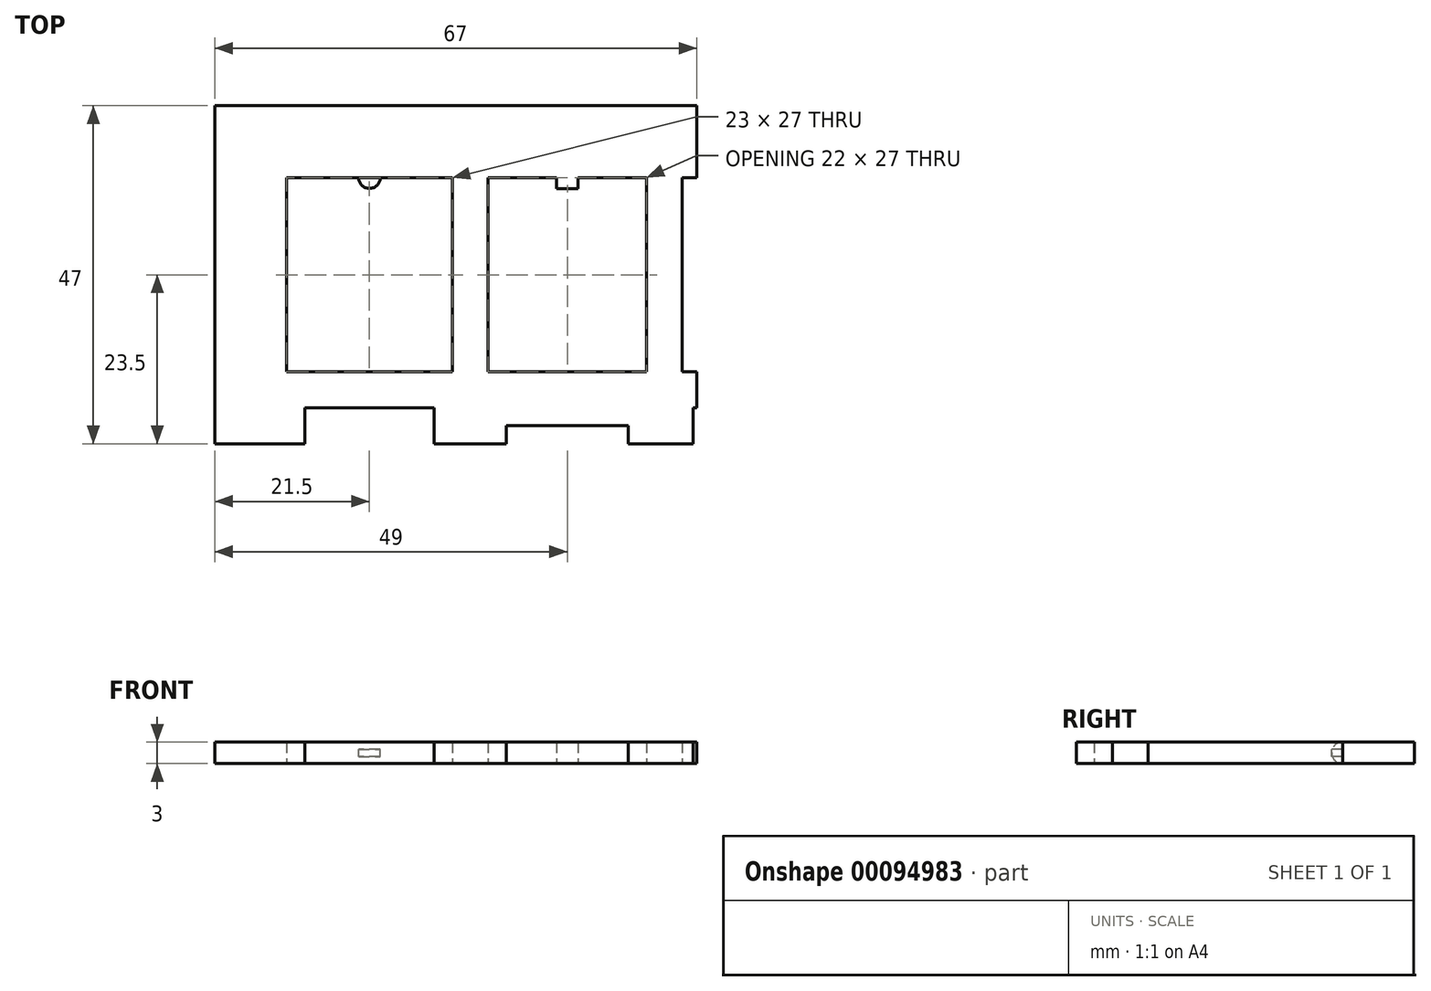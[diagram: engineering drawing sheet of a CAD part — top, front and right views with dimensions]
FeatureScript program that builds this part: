
annotation { "Feature Type Name" : "Feature", "Feature Type Description" : "" }
export const myFeature = defineFeature(function(context is Context, id is Id, definition is map)
    precondition{}
    {
        {
            var Q0;
            Q0=qCreatedBy(makeId("Top.planeOp"),FACE);
            var sketch = newSketch(context, id + "F0", { "sketchPlane" : qUnion([Q0])});
            skLineSegment(sketch, "E0.bottom", {"start": v(59.5, -71.5) * mm, "end": v(-59.5, -71.5) * mm});
            skLineSegment(sketch, "E0.top", {"start": v(59.5, 71.5) * mm, "end": v(-59.5, 71.5) * mm});
            skLineSegment(sketch, "E0.left", {"start": v(59.5, -71.5) * mm, "end": v(59.5, 71.5) * mm});
            skLineSegment(sketch, "E0.right", {"start": v(-59.5, -71.5) * mm, "end": v(-59.5, 71.5) * mm});
            skPoint(sketch, "E0.middle", {"position": v(0, 0) * mm});
            skLineSegment(sketch, "E1.bottom", {"start": v(-26.5, 34.5) * mm, "end": v(-49.5, 34.5) * mm});
            skLineSegment(sketch, "E1.top", {"start": v(-26.5, 61.5) * mm, "end": v(-49.5, 61.5) * mm});
            skLineSegment(sketch, "E1.left", {"start": v(-26.5, 34.5) * mm, "end": v(-26.5, 61.5) * mm});
            skLineSegment(sketch, "E1.right", {"start": v(-49.5, 34.5) * mm, "end": v(-49.5, 61.5) * mm});
            skPoint(sketch, "E1.middle", {"position": v(-38, 48) * mm});
            skLineSegment(sketch, "E2.bottom", {"start": v(0.5, 34.5) * mm, "end": v(-21.5, 34.5) * mm});
            skLineSegment(sketch, "E2.top", {"start": v(0.5, 61.5) * mm, "end": v(-21.5, 61.5) * mm});
            skLineSegment(sketch, "E2.left", {"start": v(0.5, 34.5) * mm, "end": v(0.5, 61.5) * mm});
            skLineSegment(sketch, "E2.right", {"start": v(-21.5, 34.5) * mm, "end": v(-21.5, 61.5) * mm});
            skPoint(sketch, "E2.middle", {"position": v(-10.5, 48) * mm});
            skLineSegment(sketch, "E3.bottom", {"start": v(5.5, 61.5) * mm, "end": v(26.5, 61.5) * mm});
            skLineSegment(sketch, "E3.top", {"start": v(5.5, 34.5) * mm, "end": v(26.5, 34.5) * mm});
            skLineSegment(sketch, "E3.left", {"start": v(5.5, 61.5) * mm, "end": v(5.5, 34.5) * mm});
            skLineSegment(sketch, "E3.right", {"start": v(26.5, 61.5) * mm, "end": v(26.5, 34.5) * mm});
            skLineSegment(sketch, "E4.bottom", {"start": v(31.5, 61.5) * mm, "end": v(49.5, 61.5) * mm});
            skLineSegment(sketch, "E4.top", {"start": v(31.5, 34.5) * mm, "end": v(49.5, 34.5) * mm});
            skLineSegment(sketch, "E4.left", {"start": v(31.5, 61.5) * mm, "end": v(31.5, 34.5) * mm});
            skLineSegment(sketch, "E4.right", {"start": v(49.5, 61.5) * mm, "end": v(49.5, 34.5) * mm});
            skLineSegment(sketch, "E5.bottom", {"start": v(33, 27) * mm, "end": v(48, 27) * mm});
            skLineSegment(sketch, "E5.top", {"start": v(33, 5) * mm, "end": v(48, 5) * mm});
            skLineSegment(sketch, "E5.left", {"start": v(33, 27) * mm, "end": v(33, 5) * mm});
            skLineSegment(sketch, "E5.right", {"start": v(48, 27) * mm, "end": v(48, 5) * mm});
            skPoint(sketch, "E6", {"position": v(40.5, 48) * mm});
            skPoint(sketch, "E6.positionSnap0", {"position": v(40.5, 34.5) * mm});
            skPoint(sketch, "E6.positionSnap1", {"position": v(49.5, 48) * mm});
            skPoint(sketch, "E7", {"position": v(16, 48) * mm});
            skPoint(sketch, "E7.positionSnap0", {"position": v(16, 34.5) * mm});
            skPoint(sketch, "E8", {"position": v(40.5, 16) * mm});
            skPoint(sketch, "E8.positionSnap0", {"position": v(40.5, 5) * mm});
            skPoint(sketch, "E8.positionSnap1", {"position": v(48, 16) * mm});
            skLineSegment(sketch, "E9.bottom", {"start": v(-19, 27) * mm, "end": v(-2, 27) * mm});
            skLineSegment(sketch, "E9.top", {"start": v(-19, 5) * mm, "end": v(-2, 5) * mm});
            skLineSegment(sketch, "E9.left", {"start": v(-19, 27) * mm, "end": v(-19, 5) * mm});
            skLineSegment(sketch, "E9.right", {"start": v(-2, 27) * mm, "end": v(-2, 5) * mm});
            skPoint(sketch, "E10", {"position": v(-10.5, 16) * mm});
            skPoint(sketch, "E10.positionSnap0", {"position": v(-2, 16) * mm});
            skPoint(sketch, "E10.positionSnap1", {"position": v(-10.5, 5) * mm});
            skLineSegment(sketch, "E11.bottom", {"start": v(-47, 29.5) * mm, "end": v(-29, 29.5) * mm});
            skLineSegment(sketch, "E11.top", {"start": v(-47, 2.5) * mm, "end": v(-29, 2.5) * mm});
            skLineSegment(sketch, "E11.left", {"start": v(-47, 29.5) * mm, "end": v(-47, 2.5) * mm});
            skLineSegment(sketch, "E11.right", {"start": v(-29, 29.5) * mm, "end": v(-29, 2.5) * mm});
            skPoint(sketch, "E12", {"position": v(-38, 16) * mm});
            skPoint(sketch, "E12.positionSnap0", {"position": v(-29, 16) * mm});
            skPoint(sketch, "E12.positionSnap1", {"position": v(-38, 2.5) * mm});
            skLineSegment(sketch, "E13.bottom", {"start": v(7, 29.5) * mm, "end": v(25, 29.5) * mm});
            skLineSegment(sketch, "E13.top", {"start": v(7, 2.5) * mm, "end": v(25, 2.5) * mm});
            skLineSegment(sketch, "E13.left", {"start": v(7, 29.5) * mm, "end": v(7, 2.5) * mm});
            skLineSegment(sketch, "E13.right", {"start": v(25, 29.5) * mm, "end": v(25, 2.5) * mm});
            skPoint(sketch, "E14", {"position": v(16, 16) * mm});
            skPoint(sketch, "E14.positionSnap0", {"position": v(25, 16) * mm});
            skPoint(sketch, "E14.positionSnap1", {"position": v(16, 2.5) * mm});
            skLineSegment(sketch, "E15.bottom", {"start": v(-45, -5) * mm, "end": v(-31, -5) * mm});
            skLineSegment(sketch, "E15.top", {"start": v(-45, -27) * mm, "end": v(-31, -27) * mm});
            skLineSegment(sketch, "E15.left", {"start": v(-45, -5) * mm, "end": v(-45, -27) * mm});
            skLineSegment(sketch, "E15.right", {"start": v(-31, -5) * mm, "end": v(-31, -27) * mm});
            skLineSegment(sketch, "E16.bottom", {"start": v(9.58, -5) * mm, "end": v(22.58, -5) * mm});
            skLineSegment(sketch, "E16.top", {"start": v(9.58, -27) * mm, "end": v(22.58, -27) * mm});
            skLineSegment(sketch, "E16.left", {"start": v(9.58, -5) * mm, "end": v(9.58, -27) * mm});
            skLineSegment(sketch, "E16.right", {"start": v(22.58, -5) * mm, "end": v(22.58, -27) * mm});
            skPoint(sketch, "E17.firstSnap0", {"position": v(16.08, -5) * mm});
            skLineSegment(sketch, "E17.bottom", {"start": v(34.82, -5) * mm, "end": v(47.82, -5) * mm});
            skLineSegment(sketch, "E17.top", {"start": v(34.82, -27) * mm, "end": v(47.82, -27) * mm});
            skLineSegment(sketch, "E17.left", {"start": v(34.82, -5) * mm, "end": v(34.82, -27) * mm});
            skLineSegment(sketch, "E17.right", {"start": v(47.82, -5) * mm, "end": v(47.82, -27) * mm});
            skPoint(sketch, "E18", {"position": v(-38, -16) * mm});
            skPoint(sketch, "E18.positionSnap0", {"position": v(-31, -16) * mm});
            skPoint(sketch, "E18.positionSnap1", {"position": v(-38, -27) * mm});
            skPoint(sketch, "E19", {"position": v(16.08, -16) * mm});
            skPoint(sketch, "E19.positionSnap0", {"position": v(22.58, -16) * mm});
            skPoint(sketch, "E19.positionSnap1", {"position": v(16.08, -27) * mm});
            skPoint(sketch, "E20", {"position": v(41.32, -16) * mm});
            skPoint(sketch, "E20.positionSnap0", {"position": v(47.82, -16) * mm});
            skPoint(sketch, "E20.positionSnap1", {"position": v(41.32, -27) * mm});
            skLineSegment(sketch, "E21.bottom", {"start": v(-17, -5) * mm, "end": v(-4, -5) * mm});
            skLineSegment(sketch, "E21.top", {"start": v(-17, -27) * mm, "end": v(-4, -27) * mm});
            skLineSegment(sketch, "E21.left", {"start": v(-17, -5) * mm, "end": v(-17, -27) * mm});
            skLineSegment(sketch, "E21.right", {"start": v(-4, -5) * mm, "end": v(-4, -27) * mm});
            skPoint(sketch, "E22", {"position": v(-10.5, -16) * mm});
            skPoint(sketch, "E22.positionSnap0", {"position": v(-4, -16) * mm});
            skPoint(sketch, "E22.positionSnap1", {"position": v(-10.5, -27) * mm});
            skLineSegment(sketch, "E23.bottom", {"start": v(-44.5, -37) * mm, "end": v(-31.5, -37) * mm});
            skLineSegment(sketch, "E23.top", {"start": v(-44.5, -59) * mm, "end": v(-31.5, -59) * mm});
            skLineSegment(sketch, "E23.left", {"start": v(-44.5, -37) * mm, "end": v(-44.5, -59) * mm});
            skLineSegment(sketch, "E23.right", {"start": v(-31.5, -37) * mm, "end": v(-31.5, -59) * mm});
            skLineSegment(sketch, "E24.bottom", {"start": v(-17, -37) * mm, "end": v(-4, -37) * mm});
            skLineSegment(sketch, "E24.top", {"start": v(-17, -59) * mm, "end": v(-4, -59) * mm});
            skLineSegment(sketch, "E24.left", {"start": v(-17, -37) * mm, "end": v(-17, -59) * mm});
            skLineSegment(sketch, "E24.right", {"start": v(-4, -37) * mm, "end": v(-4, -59) * mm});
            skLineSegment(sketch, "E25.bottom", {"start": v(9.58, -37) * mm, "end": v(22.58, -37) * mm});
            skLineSegment(sketch, "E25.top", {"start": v(9.58, -59) * mm, "end": v(22.58, -59) * mm});
            skLineSegment(sketch, "E25.left", {"start": v(9.58, -37) * mm, "end": v(9.58, -59) * mm});
            skLineSegment(sketch, "E25.right", {"start": v(22.58, -37) * mm, "end": v(22.58, -59) * mm});
            skLineSegment(sketch, "E26.bottom", {"start": v(34.82, -37) * mm, "end": v(47.82, -37) * mm});
            skLineSegment(sketch, "E26.top", {"start": v(34.82, -59) * mm, "end": v(47.82, -59) * mm});
            skLineSegment(sketch, "E26.left", {"start": v(34.82, -37) * mm, "end": v(34.82, -59) * mm});
            skLineSegment(sketch, "E26.right", {"start": v(47.82, -37) * mm, "end": v(47.82, -59) * mm});
            skPoint(sketch, "E27", {"position": v(-38, -48) * mm});
            skPoint(sketch, "E27.positionSnap0", {"position": v(-31.5, -48) * mm});
            skPoint(sketch, "E27.positionSnap1", {"position": v(-38, -59) * mm});
            skPoint(sketch, "E28", {"position": v(-10.5, -48) * mm});
            skPoint(sketch, "E28.positionSnap0", {"position": v(-10.5, -59) * mm});
            skPoint(sketch, "E28.positionSnap1", {"position": v(-4, -48) * mm});
            skPoint(sketch, "E29", {"position": v(16.08, -48) * mm});
            skPoint(sketch, "E29.positionSnap0", {"position": v(22.58, -48) * mm});
            skPoint(sketch, "E29.positionSnap1", {"position": v(16.08, -59) * mm});
            skPoint(sketch, "E30", {"position": v(41.32, -48) * mm});
            skPoint(sketch, "E30.positionSnap0", {"position": v(47.82, -48) * mm});
            skPoint(sketch, "E30.positionSnap1", {"position": v(41.32, -59) * mm});
            skPoint(sketch, "E31", {"position": v(-44.5, -49.5) * mm});
            skPoint(sketch, "E32", {"position": v(-17, -48.5) * mm});
            skPoint(sketch, "E33", {"position": v(9.58, -48.5) * mm});
            skPoint(sketch, "E34", {"position": v(34.82, -48.5) * mm});
            skLineSegment(sketch, "E35", {"start": v(-42.75, -50.27) * mm, "end": v(-33.25, -50.27) * mm});
            skPoint(sketch, "E36", {"position": v(-38, -50.27) * mm});
            skLineSegment(sketch, "E37", {"start": v(-15.25, -51.11) * mm, "end": v(-5.75, -51.11) * mm});
            skPoint(sketch, "E38", {"position": v(-10.5, -51.11) * mm});
            skLineSegment(sketch, "E39", {"start": v(11.58, -50.9) * mm, "end": v(20.58, -50.9) * mm});
            skPoint(sketch, "E40", {"position": v(16.08, -50.9) * mm});
            skLineSegment(sketch, "E41", {"start": v(36.82, -50.7) * mm, "end": v(45.82, -50.7) * mm});
            skPoint(sketch, "E42", {"position": v(41.32, -50.7) * mm});
            skPoint(sketch, "E43", {"position": v(7.5, 71.5) * mm});
            skPoint(sketch, "E44", {"position": v(-59.5, 24.5) * mm});
            skLineSegment(sketch, "E45", {"start": v(-59.5, 24.5) * mm, "end": v(7.5, 24.5) * mm});
            skLineSegment(sketch, "E46", {"start": v(7.5, 24.5) * mm, "end": v(7.5, 71.5) * mm});
            skSolve(sketch);
        }
        {
            var Q0;
            Q0=makeQuery(id+"F0.imprint","IMPRINT",FACE,{"disambiguationData":[TD([[makeQuery(id+"F0.imprint","IMPRINT",EDGE,{"derivedFrom":sQuery(id+"F0.wireOp",EDGE,"E1.bottom")}),1.0]])]});
            extrude(context, id + "F1", {"entities" : qUnion([Q0]), "depth" : 3 * mm});
        }
        {
            var Q0;
            Q0=makeQuery(id+"F1.opExtrude","SWEPT_FACE",FACE,{"disambiguationData":[OSD([sQuery(id+"F0.wireOp",EDGE,"E1.top")])]});
            var sketch = newSketch(context, id + "F2", { "sketchPlane" : qUnion([Q0])});
            skLineSegment(sketch, "E47", {"start": v(-49.5, 3) * mm, "end": v(-26.5, 3) * mm});
            skPoint(sketch, "E48", {"position": v(-38, 3) * mm});
            skLineSegment(sketch, "E49", {"start": v(-38, 3) * mm, "end": v(-38, 0) * mm});
            skPoint(sketch, "E50", {"position": v(-38, 1.5) * mm});
            skLineSegment(sketch, "E51.bottom", {"start": v(-38, 2) * mm, "end": v(-36.5, 2) * mm});
            skLineSegment(sketch, "E51.top", {"start": v(-38, 1) * mm, "end": v(-36.5, 1) * mm});
            skLineSegment(sketch, "E51.left", {"start": v(-38, 2) * mm, "end": v(-38, 1) * mm});
            skLineSegment(sketch, "E51.right", {"start": v(-36.5, 2) * mm, "end": v(-36.5, 1) * mm});
            skSolve(sketch);
        }
        {
            var Q0;
            Q0=makeQuery(id+"F2.imprint","IMPRINT",FACE,{"disambiguationData":[TD([[makeQuery(id+"F2.imprint","IMPRINT",EDGE,{"derivedFrom":sQuery(id+"F2.wireOp",EDGE,"E51.bottom")}),-1.0]])]});
            var Q1;
            Q1=sQuery(id+"F2.wireOp",EDGE,"E49");
            revolve(context, id + "F3", {"operationType" : NewBodyOperationType.ADD, "entities" : qUnion([Q0]), "axis" : qUnion([Q1]), "revolveType" : RevolveType.FULL});
        }
        {
            var Q0;
            Q0=makeQuery(id+"F1.opExtrude","SWEPT_FACE",FACE,{"disambiguationData":[OSD([sQuery(id+"F0.wireOp",EDGE,"E2.top")])]});
            var sketch = newSketch(context, id + "F4", { "sketchPlane" : qUnion([Q0])});
            skLineSegment(sketch, "E52", {"start": v(-10.5, 3) * mm, "end": v(-10.5, 0) * mm});
            skPoint(sketch, "E53", {"position": v(-10.5, 1.5) * mm});
            skPoint(sketch, "E54", {"position": v(0.5, 1.5) * mm});
            skLineSegment(sketch, "E55", {"start": v(0.5, 1.5) * mm, "end": v(-21.5, 1.5) * mm});
            skLineSegment(sketch, "E56", {"start": v(-10.5, 3) * mm, "end": v(-10.5, 1.5) * mm});
            skPoint(sketch, "E57", {"position": v(-10.5, 2.25) * mm});
            skLineSegment(sketch, "E58.bottom", {"start": v(-9.04, 3) * mm, "end": v(-11.96, 3) * mm});
            skLineSegment(sketch, "E58.top", {"start": v(-9.04, 1.5) * mm, "end": v(-11.96, 1.5) * mm});
            skLineSegment(sketch, "E58.left", {"start": v(-9.04, 3) * mm, "end": v(-9.04, 1.5) * mm});
            skLineSegment(sketch, "E58.right", {"start": v(-11.96, 3) * mm, "end": v(-11.96, 1.5) * mm});
            skSolve(sketch);
        }
        {
            var Q0;
            {var subQ5=sQuery(id+"F4.wireOp",EDGE,"E58.right");Q0=makeQuery(id+"F4.imprint","IMPRINT",FACE,{"disambiguationData":[TD([[makeQuery(id+"F4.imprint","IMPRINT",EDGE,{"derivedFrom":subQ5}),1.0]])]});}
            var Q1;
            {var subQ5=sQuery(id+"F4.wireOp",EDGE,"E58.left");Q1=makeQuery(id+"F4.imprint","IMPRINT",FACE,{"disambiguationData":[TD([[makeQuery(id+"F4.imprint","IMPRINT",EDGE,{"derivedFrom":subQ5}),-1.0]])]});}
            var Q2;
            Q2=sQuery(id+"F4.wireOp",EDGE,"E55");
            revolve(context, id + "F5", {"operationType" : NewBodyOperationType.ADD, "entities" : qUnion([Q0, Q1]), "axis" : qUnion([Q2]), "revolveType" : RevolveType.FULL});
        }
    });
